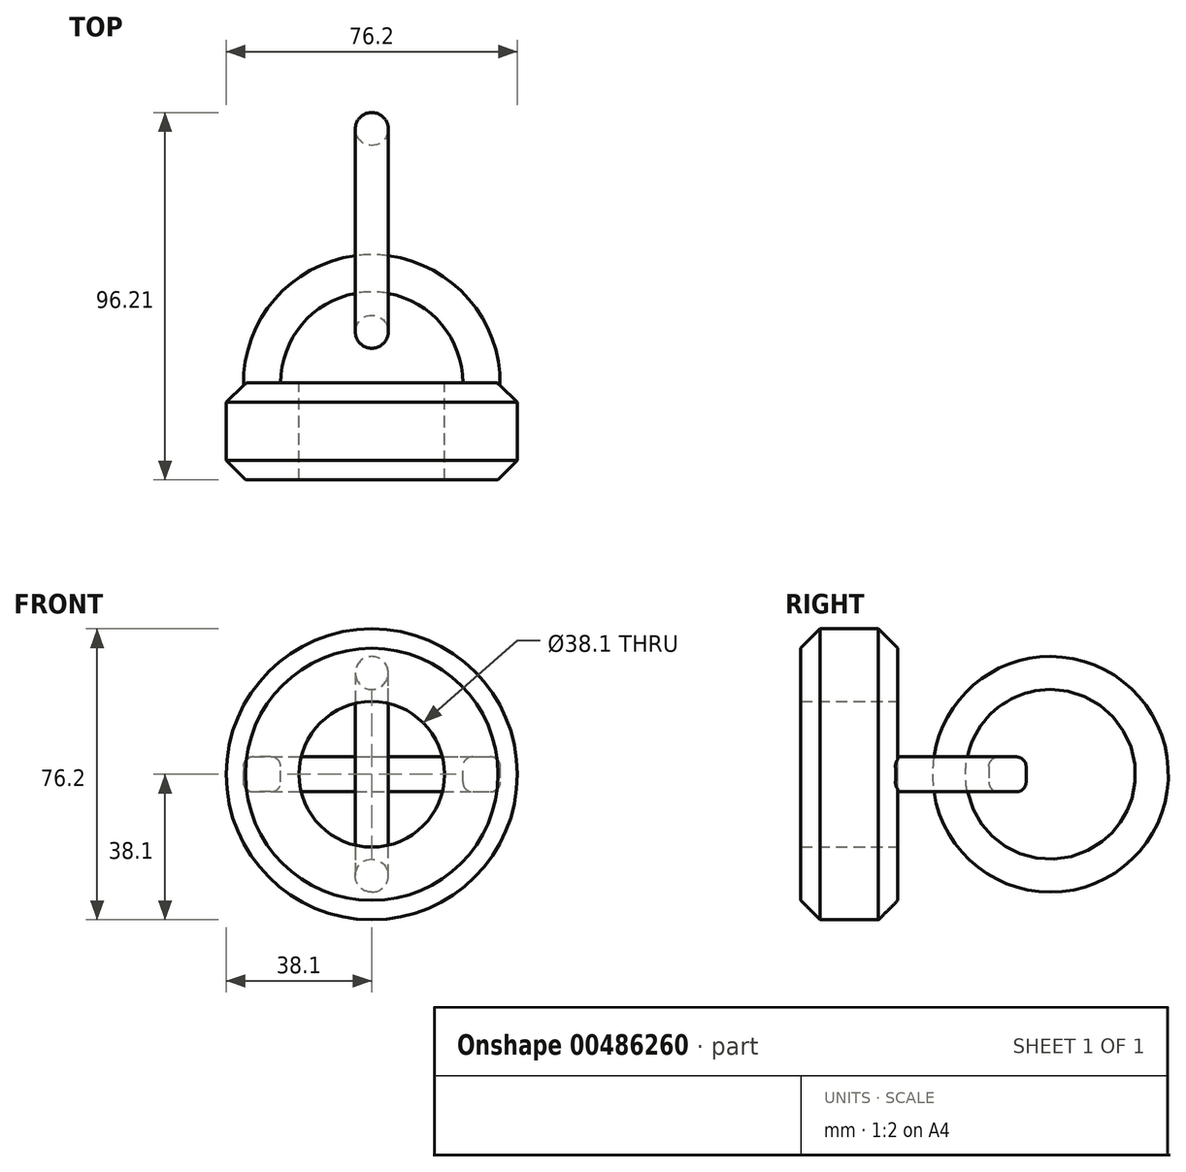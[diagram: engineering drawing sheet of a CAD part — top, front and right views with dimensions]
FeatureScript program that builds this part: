
annotation { "Feature Type Name" : "Feature", "Feature Type Description" : "" }
export const myFeature = defineFeature(function(context is Context, id is Id, definition is map)
    precondition{}
    {
        {
            var Q0;
            Q0=qCreatedBy(makeId("Front.planeOp"),FACE);
            var sketch = newSketch(context, id + "F0", { "sketchPlane" : qUnion([Q0])});
            skCircle(sketch, "E0", {"center": v(0, 0) * mm, "radius": 38.1 * mm});
            skCircle(sketch, "E1", {"center": v(0, 0) * mm, "radius": 19.05 * mm});
            skSolve(sketch);
        }
        {
            var Q0;
            Q0=makeQuery(id+"F0.imprint","IMPRINT",FACE,{"disambiguationData":[TD([[makeQuery(id+"F0.imprint","IMPRINT",EDGE,{"derivedFrom":sQuery(id+"F0.wireOp",EDGE,"E0")}),1.0]])]});
            var Q1;
            Q1=sQuery(id+"F0.wireOp",EDGE,"E1");
            var Q2;
            Q2=sQuery(id+"F0.wireOp",EDGE,"E0");
            extrude(context, id + "F1", {"entities" : qUnion([Q0]), "surfaceEntities" : qUnion([Q1, Q2]), "depth" : 25.4 * mm});
        }
        {
            var Q0;
            Q0=makeQuery(id+"F1.opExtrude","CAP_FACE",FACE,{"disambiguationData":[OSD([sQuery(id+"F0.wireOp",EDGE,"E0"),sQuery(id+"F0.wireOp",EDGE,"E1")])],"isStart":true});
            var sketch = newSketch(context, id + "F2", { "sketchPlane" : qUnion([Q0])});
            skLineSegment(sketch, "E2.bottom", {"start": v(-23.85, -4.58) * mm, "end": v(-33.58, -4.58) * mm});
            skLineSegment(sketch, "E2.top", {"start": v(-23.85, 4.58) * mm, "end": v(-33.58, 4.58) * mm});
            skLineSegment(sketch, "E2.left", {"start": v(-23.85, -4.58) * mm, "end": v(-23.85, 4.58) * mm});
            skLineSegment(sketch, "E2.right", {"start": v(-33.58, -4.58) * mm, "end": v(-33.58, 4.58) * mm});
            skPoint(sketch, "E2.middle", {"position": v(-28.72, 0) * mm});
            skLineSegment(sketch, "E3", {"start": v(0, 28.37) * mm, "end": v(0, -28.04) * mm});
            skSolve(sketch);
        }
        {
            var Q0;
            Q0 = qSketchRegion(id + "F2", true);
            var Q1;
            Q1=makeQuery(id+"F2.imprint","IMPRINT",FACE,{"disambiguationData":[TD([[makeQuery(id+"F2.imprint","IMPRINT",EDGE,{"derivedFrom":sQuery(id+"F2.wireOp",EDGE,"E2.bottom")}),-1.0]])]});
            var Q2;
            Q2=sQuery(id+"F2.wireOp",EDGE,"E3");
            revolve(context, id + "F3", {"operationType" : NewBodyOperationType.ADD, "entities" : qUnion([Q0, Q1]), "axis" : qUnion([Q2]), "revolveType" : RevolveType.ONE_DIRECTION, "oppositeDirection" : true, "angle" : 180 * degree});
        }
        {
            var Q0;
            Q0=makeQuery(id+"F3.opRevolve","SWEPT_EDGE",EDGE,{"disambiguationData":[OSD([sQuery(id+"F2.wireOp",EDGE,"E2.bottom"),sQuery(id+"F2.wireOp",EDGE,"E2.left")])]});
            var Q1;
            Q1=makeQuery(id+"F3.opRevolve","SWEPT_EDGE",EDGE,{"disambiguationData":[OSD([sQuery(id+"F2.wireOp",EDGE,"E2.bottom"),sQuery(id+"F2.wireOp",EDGE,"E2.right")])]});
            fillet(context, id + "F4", {"entities" : qUnion([Q0, Q1]), "radius" : 2.54 * mm, "allowEdgeOverflow" : false});
        }
        {
            var Q0;
            Q0=makeQuery(id+"F3.opRevolve","SWEPT_EDGE",EDGE,{"disambiguationData":[OSD([sQuery(id+"F2.wireOp",EDGE,"E2.top"),sQuery(id+"F2.wireOp",EDGE,"E2.left")])]});
            var Q1;
            Q1=makeQuery(id+"F3.opRevolve","SWEPT_EDGE",EDGE,{"disambiguationData":[OSD([sQuery(id+"F2.wireOp",EDGE,"E2.top"),sQuery(id+"F2.wireOp",EDGE,"E2.right")])]});
            fillet(context, id + "F5", {"entities" : qUnion([Q0, Q1]), "radius" : 2.54 * mm, "tangentPropagation" : true, "allowEdgeOverflow" : false});
        }
        {
            var Q0;
            Q0=makeQuery(id+"F1.opExtrude","CAP_EDGE",EDGE,{"disambiguationData":[OSD([sQuery(id+"F0.wireOp",EDGE,"E0")])],"isStart":false});
            chamfer(context, id + "F6", {"entities" : qUnion([Q0]), "width" : 5.08 * mm, "tangentPropagation" : true});
        }
        {
            var Q0;
            Q0=makeQuery(id+"F1.opExtrude","CAP_EDGE",EDGE,{"disambiguationData":[OSD([sQuery(id+"F0.wireOp",EDGE,"E0")])],"isStart":true});
            chamfer(context, id + "F7", {"entities" : qUnion([Q0]), "width" : 5.08 * mm, "tangentPropagation" : true});
        }
        {
            var Q0;
            Q0=qCreatedBy(makeId("Top.planeOp"),FACE);
            var sketch = newSketch(context, id + "F8", { "sketchPlane" : qUnion([Q0])});
            skCircle(sketch, "E4", {"center": v(0, 13.41) * mm, "radius": 4.32 * mm});
            skLineSegment(sketch, "E5", {"start": v(23.31, 37.62) * mm, "end": v(23.31, 37.62) * mm});
            skLineSegment(sketch, "E6", {"start": v(-12.36, 39.95) * mm, "end": v(12.2, 39.95) * mm});
            skSolve(sketch);
        }
        {
            var Q0;
            Q0=makeQuery(id+"F8.imprint","IMPRINT",FACE,{"disambiguationData":[TD([[makeQuery(id+"F8.imprint","IMPRINT",EDGE,{"derivedFrom":sQuery(id+"F8.wireOp",EDGE,"E4")}),1.0]])]});
            var Q1;
            Q1=sQuery(id+"F8.wireOp",EDGE,"E6");
            revolve(context, id + "F9", {"entities" : qUnion([Q0]), "axis" : qUnion([Q1]), "revolveType" : RevolveType.FULL});
        }
    });
